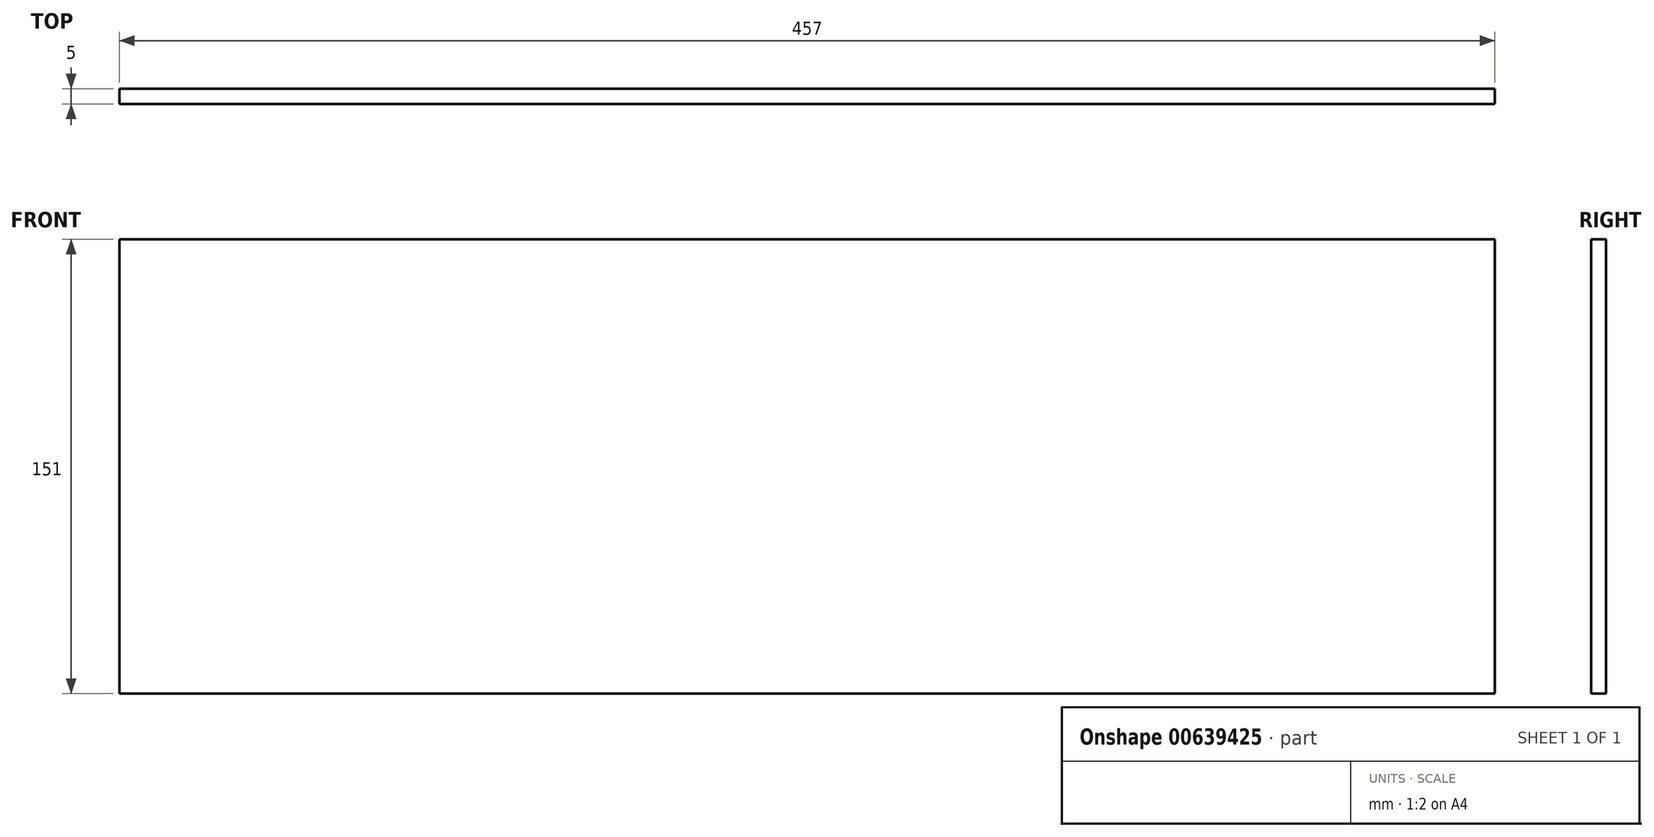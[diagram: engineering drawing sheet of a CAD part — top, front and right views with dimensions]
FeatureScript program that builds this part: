
annotation { "Feature Type Name" : "Feature", "Feature Type Description" : "" }
export const myFeature = defineFeature(function(context is Context, id is Id, definition is map)
    precondition{}
    {
        {
            var Q0;
            Q0=qCreatedBy(makeId("Front.planeOp"),FACE);
            var sketch = newSketch(context, id + "F0", { "sketchPlane" : qUnion([Q0])});
            skLineSegment(sketch, "E0.bottom", {"start": v(0, 0) * mm, "end": v(457, 0) * mm});
            skLineSegment(sketch, "E0.top", {"start": v(0, 151) * mm, "end": v(457, 151) * mm});
            skLineSegment(sketch, "E0.left", {"start": v(0, 0) * mm, "end": v(0, 151) * mm});
            skLineSegment(sketch, "E0.right", {"start": v(457, 0) * mm, "end": v(457, 151) * mm});
            skSolve(sketch);
        }
        {
            var Q0;
            Q0=makeQuery(id+"F0.imprint","IMPRINT",FACE,{"disambiguationData":[TD([[makeQuery(id+"F0.imprint","IMPRINT",EDGE,{"derivedFrom":sQuery(id+"F0.wireOp",EDGE,"E0.bottom")}),1.0]])]});
            extrude(context, id + "F1", {"entities" : qUnion([Q0]), "depth" : 5 * mm, "offsetDistance" : 25 * mm});
        }
    });
